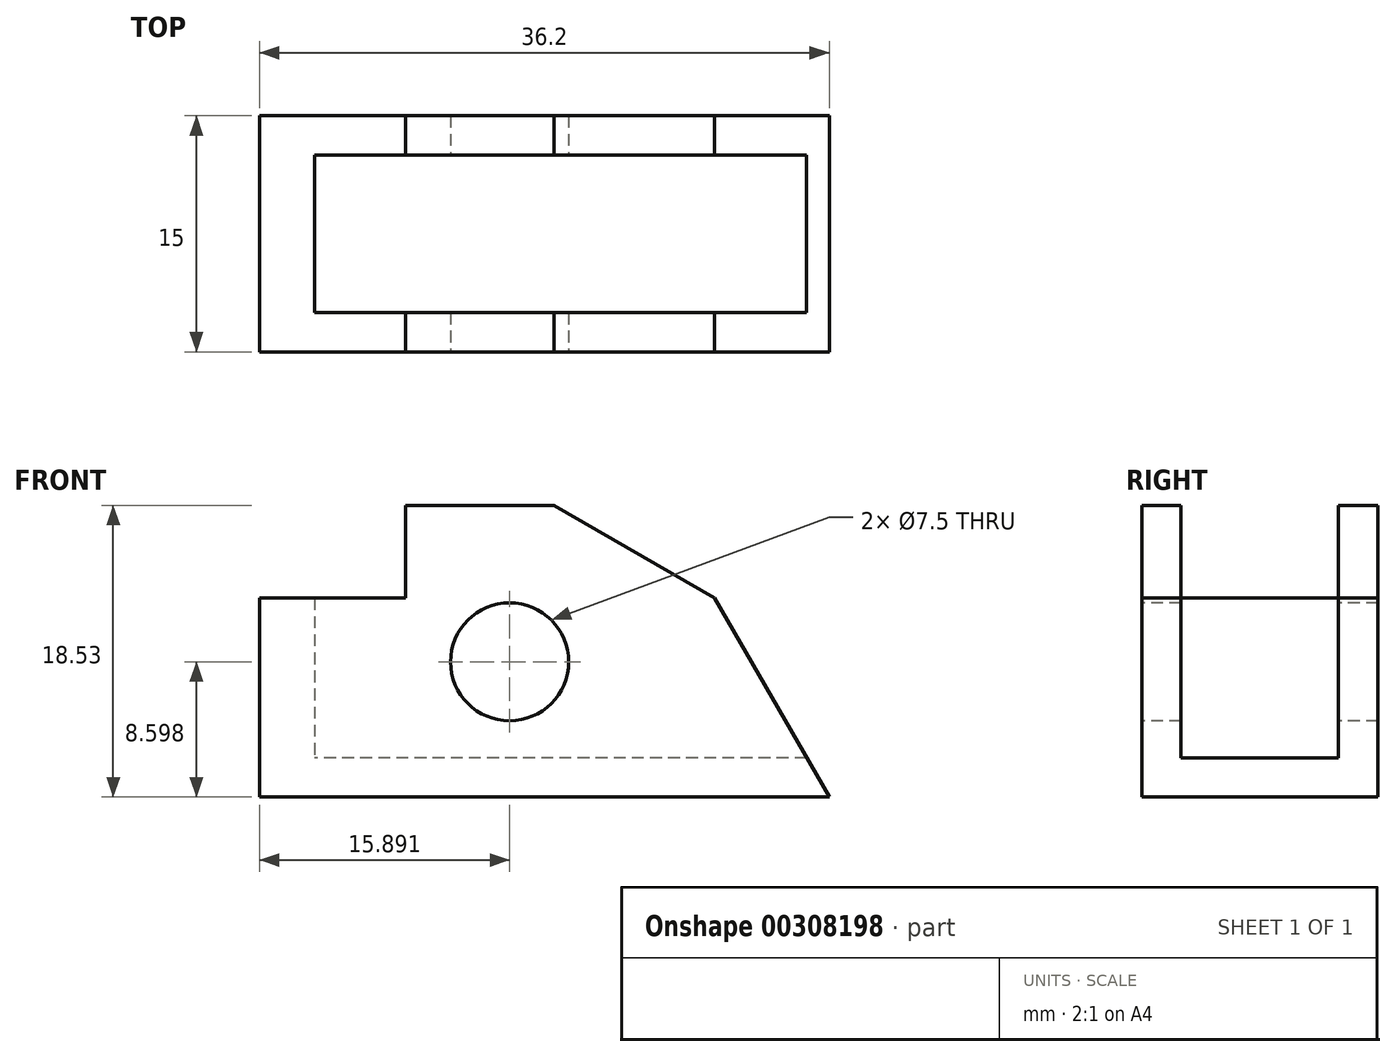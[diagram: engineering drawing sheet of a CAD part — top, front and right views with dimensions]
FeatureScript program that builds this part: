
annotation { "Feature Type Name" : "Feature", "Feature Type Description" : "" }
export const myFeature = defineFeature(function(context is Context, id is Id, definition is map)
    precondition{}
    {
        {
            var Q0;
            Q0=qCreatedBy(makeId("Front.planeOp"),FACE);
            var sketch = newSketch(context, id + "F0", { "sketchPlane" : qUnion([Q0])});
            skLineSegment(sketch, "E0", {"start": v(0, 0) * mm, "end": v(0, 12.64) * mm});
            skLineSegment(sketch, "E1", {"start": v(0, 12.64) * mm, "end": v(9.29, 12.64) * mm});
            skLineSegment(sketch, "E2", {"start": v(9.29, 12.64) * mm, "end": v(9.29, 18.53) * mm});
            skLineSegment(sketch, "E3", {"start": v(9.29, 18.53) * mm, "end": v(18.7, 18.53) * mm});
            skLineSegment(sketch, "E4", {"start": v(18.7, 18.53) * mm, "end": v(28.9, 12.64) * mm});
            skLineSegment(sketch, "E5", {"start": v(28.9, 12.64) * mm, "end": v(36.2, 0) * mm});
            skLineSegment(sketch, "E6", {"start": v(36.2, 0) * mm, "end": v(0, 0) * mm});
            skSolve(sketch);
        }
        {
            var Q0;
            Q0=makeQuery(id+"F0.imprint","IMPRINT",FACE,{"disambiguationData":[TD([[makeQuery(id+"F0.imprint","IMPRINT",EDGE,{"derivedFrom":sQuery(id+"F0.wireOp",EDGE,"E0")}),-1.0]])]});
            extrude(context, id + "F1", {"entities" : qUnion([Q0]), "depth" : 15 * mm});
        }
        {
            var Q0;
            Q0=makeQuery(id+"F1.opExtrude","SWEPT_FACE",FACE,{"disambiguationData":[OSD([sQuery(id+"F0.wireOp",EDGE,"E0")])]});
            var sketch = newSketch(context, id + "F2", { "sketchPlane" : qUnion([Q0])});
            skLineSegment(sketch, "E7", {"start": v(2.5, 2.5) * mm, "end": v(12.5, 2.5) * mm});
            skLineSegment(sketch, "E8", {"start": v(12.5, 2.5) * mm, "end": v(12.5, 23.04) * mm});
            skLineSegment(sketch, "E9", {"start": v(12.5, 23.04) * mm, "end": v(2.5, 23.04) * mm});
            skLineSegment(sketch, "E10", {"start": v(2.5, 23.04) * mm, "end": v(2.5, 2.5) * mm});
            skSolve(sketch);
        }
        {
            var Q0;
            {var subQ0=sQuery(id+"F2.wireOp",EDGE,"E9");Q0=makeQuery(id+"F2.imprint","IMPRINT",FACE,{"disambiguationData":[TD([[makeQuery(id+"F2.imprint","IMPRINT",EDGE,{"derivedFrom":subQ0}),1.0]])]});}
            var Q1;
            {var subQ0=sQuery(id+"F2.wireOp",EDGE,"E7");Q1=makeQuery(id+"F2.imprint","IMPRINT",FACE,{"disambiguationData":[TD([[makeQuery(id+"F2.imprint","IMPRINT",EDGE,{"derivedFrom":subQ0}),1.0]])]});}
            extrude(context, id + "F3", {"entities" : qUnion([Q0, Q1]), "operationType" : NewBodyOperationType.REMOVE, "oppositeDirection" : true, "depth" : 40 * mm});
        }
        {
            var Q0;
            Q0=makeQuery(id+"F3.boolean.opBoolean","COPY",FACE,{"derivedFrom":makeQuery(id+"F3.opExtrude","SWEPT_FACE",FACE,{"disambiguationData":[OSD([sQuery(id+"F2.wireOp",EDGE,"E7")])]})});
            var sketch = newSketch(context, id + "F4", { "sketchPlane" : qUnion([Q0])});
            skLineSegment(sketch, "E11.bottom", {"start": v(3.51, -2.5) * mm, "end": v(0, -2.5) * mm});
            skLineSegment(sketch, "E11.top", {"start": v(3.51, -12.5) * mm, "end": v(0, -12.5) * mm});
            skLineSegment(sketch, "E11.left", {"start": v(3.51, -2.5) * mm, "end": v(3.51, -12.5) * mm});
            skLineSegment(sketch, "E11.right", {"start": v(0, -2.5) * mm, "end": v(0, -12.5) * mm});
            skSolve(sketch);
        }
        {
            var Q0;
            Q0 = qSketchRegion(id + "F4", true);
            var Q1;
            {var subQ2=sQuery(id+"F0.wireOp",EDGE,"E1");Q1=makeQuery(id+"F3.boolean.opBoolean","SPLIT",FACE,{"disambiguationData":[TD([makeQuery(id+"F3.opExtrude","SWEPT_FACE",FACE,{"disambiguationData":[OSD([sQuery(id+"F2.wireOp",EDGE,"E10")])]})])],"derivedFrom":makeQuery(id+"F1.opExtrude","SWEPT_FACE",FACE,{"disambiguationData":[OSD([subQ2])]})});}
            extrude(context, id + "F5", {"entities" : qUnion([Q0]), "operationType" : NewBodyOperationType.ADD, "endBound" : BoundingType.UP_TO_SURFACE, "endBoundEntityFace" : qUnion([Q1]), "depth" : 25 * mm});
        }
        {
            var Q0;
            Q0=makeQuery(id+"F1.opExtrude","CAP_FACE",FACE,{"disambiguationData":[OSD([sQuery(id+"F0.wireOp",EDGE,"E0"),sQuery(id+"F0.wireOp",EDGE,"E1"),sQuery(id+"F0.wireOp",EDGE,"E2"),sQuery(id+"F0.wireOp",EDGE,"E3"),sQuery(id+"F0.wireOp",EDGE,"E4"),sQuery(id+"F0.wireOp",EDGE,"E5"),sQuery(id+"F0.wireOp",EDGE,"E6")])],"isStart":false});
            var sketch = newSketch(context, id + "F6", { "sketchPlane" : qUnion([Q0])});
            skCircle(sketch, "E12", {"center": v(15.9, 8.6) * mm, "radius": 3.75 * mm});
            skSolve(sketch);
        }
        {
            var Q0;
            Q0 = qSketchRegion(id + "F6", true);
            extrude(context, id + "F7", {"entities" : qUnion([Q0]), "operationType" : NewBodyOperationType.REMOVE, "oppositeDirection" : true, "depth" : 25 * mm});
        }
    });
